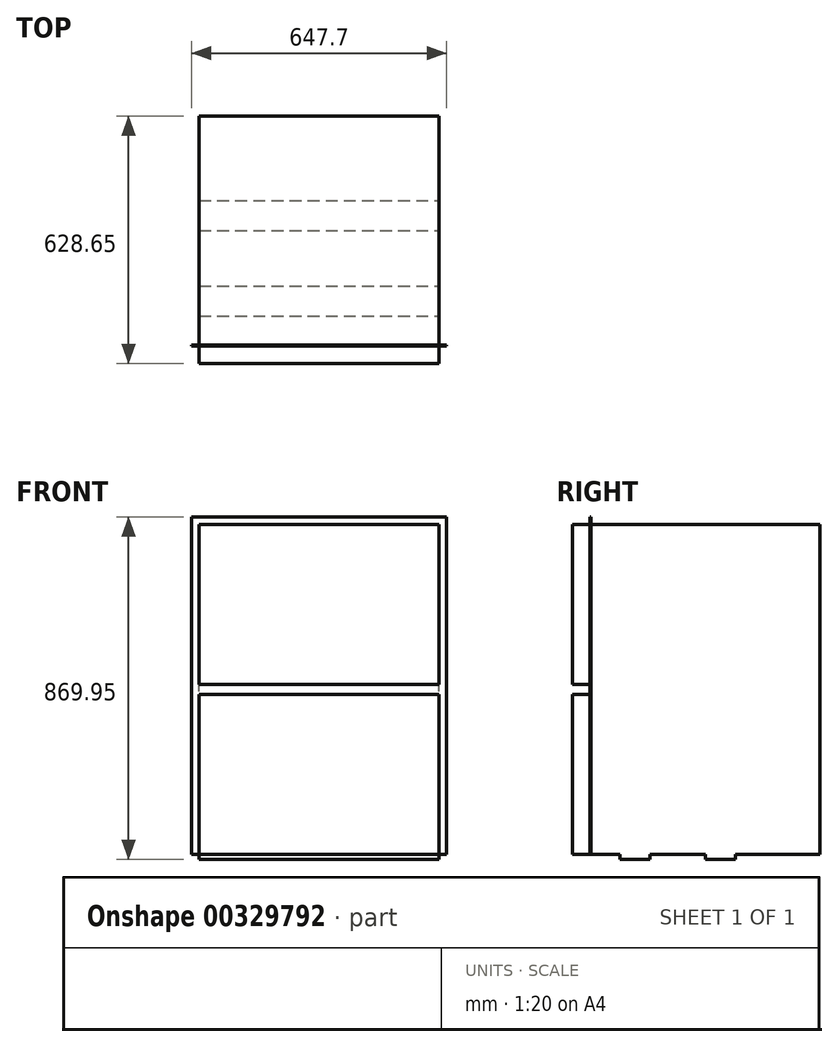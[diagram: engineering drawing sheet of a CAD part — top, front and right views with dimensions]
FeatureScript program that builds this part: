
annotation { "Feature Type Name" : "Feature", "Feature Type Description" : "" }
export const myFeature = defineFeature(function(context is Context, id is Id, definition is map)
    precondition{}
    {
        {
            var Q0;
            Q0=qCreatedBy(makeId("Front.planeOp"),FACE);
            var sketch = newSketch(context, id + "F0", { "sketchPlane" : qUnion([Q0])});
            skLineSegment(sketch, "E0.bottom", {"start": v(0, 0) * mm, "end": v(-609.6, 0) * mm});
            skLineSegment(sketch, "E0.top", {"start": v(0, 838.2) * mm, "end": v(-609.6, 838.2) * mm});
            skLineSegment(sketch, "E0.left", {"start": v(0, 0) * mm, "end": v(0, 838.2) * mm});
            skLineSegment(sketch, "E0.right", {"start": v(-609.6, 0) * mm, "end": v(-609.6, 838.2) * mm});
            skLineSegment(sketch, "E1.bottom", {"start": v(-628.65, 857.25) * mm, "end": v(19.05, 857.25) * mm});
            skLineSegment(sketch, "E1.left", {"start": v(-628.65, 857.25) * mm, "end": v(-628.65, 0) * mm});
            skLineSegment(sketch, "E1.right", {"start": v(19.05, 857.25) * mm, "end": v(19.05, 0) * mm});
            skLineSegment(sketch, "E2", {"start": v(-628.65, 0) * mm, "end": v(-609.6, 0) * mm});
            skLineSegment(sketch, "E3", {"start": v(19.05, 0) * mm, "end": v(0, 0) * mm});
            skSolve(sketch);
        }
        {
            var Q0;
            Q0=makeQuery(id+"F0.imprint","IMPRINT",FACE,{"disambiguationData":[TD([[makeQuery(id+"F0.imprint","IMPRINT",EDGE,{"derivedFrom":sQuery(id+"F0.wireOp",EDGE,"E0.bottom")}),-1.0]])]});
            extrude(context, id + "F1", {"entities" : qUnion([Q0]), "oppositeDirection" : true, "depth" : 584.2 * mm});
        }
        {
            var Q0;
            Q0=makeQuery(id+"F0.imprint","IMPRINT",FACE,{"disambiguationData":[TD([[makeQuery(id+"F0.imprint","IMPRINT",EDGE,{"derivedFrom":sQuery(id+"F0.wireOp",EDGE,"E0.top")}),-1.0]])]});
            extrude(context, id + "F2", {"entities" : qUnion([Q0]), "operationType" : NewBodyOperationType.ADD, "oppositeDirection" : true, "depth" : 2.03 * mm});
        }
        {
            var Q0;
            Q0=makeQuery(id+"F0.imprint","IMPRINT",FACE,{"disambiguationData":[TD([[makeQuery(id+"F0.imprint","IMPRINT",EDGE,{"derivedFrom":sQuery(id+"F0.wireOp",EDGE,"E0.bottom")}),-1.0]])]});
            var sketch = newSketch(context, id + "F3", { "sketchPlane" : qUnion([Q0])});
            skLineSegment(sketch, "E4.bottom", {"start": v(-609.6, 838.2) * mm, "end": v(0, 838.2) * mm});
            skLineSegment(sketch, "E4.top", {"start": v(-609.6, 431.8) * mm, "end": v(0, 431.8) * mm});
            skLineSegment(sketch, "E4.left", {"start": v(-609.6, 838.2) * mm, "end": v(-609.6, 431.8) * mm});
            skLineSegment(sketch, "E4.right", {"start": v(0, 838.2) * mm, "end": v(0, 431.8) * mm});
            skLineSegment(sketch, "E5.bottom", {"start": v(-609.6, 406.4) * mm, "end": v(0, 406.4) * mm});
            skLineSegment(sketch, "E5.top", {"start": v(-609.6, 0) * mm, "end": v(0, 0) * mm});
            skLineSegment(sketch, "E5.left", {"start": v(-609.6, 406.4) * mm, "end": v(-609.6, 0) * mm});
            skLineSegment(sketch, "E5.right", {"start": v(0, 406.4) * mm, "end": v(0, 0) * mm});
            skSolve(sketch);
        }
        {
            var Q0;
            Q0 = qSketchRegion(id + "F3", true);
            extrude(context, id + "F4", {"entities" : qUnion([Q0]), "operationType" : NewBodyOperationType.ADD, "depth" : 44.45 * mm});
        }
        {
            var Q0;
            Q0=makeQuery(id+"F4.boolean.opBoolean","MERGE",FACE,{"derivedFrom":[makeQuery(id+"F2.boolean.opBoolean","MERGE",FACE,{"derivedFrom":[makeQuery(id+"F1.opExtrude","SWEPT_FACE",FACE,{"disambiguationData":[OSD([sQuery(id+"F0.wireOp",EDGE,"E0.bottom")])]}),makeQuery(id+"F2.opExtrude","SWEPT_FACE",FACE,{"disambiguationData":[OSD([sQuery(id+"F0.wireOp",EDGE,"E2")])]}),makeQuery(id+"F2.opExtrude","SWEPT_FACE",FACE,{"disambiguationData":[OSD([sQuery(id+"F0.wireOp",EDGE,"E3")])]})]}),makeQuery(id+"F4.opExtrude","SWEPT_FACE",FACE,{"disambiguationData":[OSD([sQuery(id+"F3.wireOp",EDGE,"E5.top")])]})]});
            var sketch = newSketch(context, id + "F5", { "sketchPlane" : qUnion([Q0])});
            skLineSegment(sketch, "E6.bottom", {"start": v(-609.6, -75.96) * mm, "end": v(0, -75.96) * mm});
            skLineSegment(sketch, "E6.top", {"start": v(-609.6, -152.16) * mm, "end": v(0, -152.16) * mm});
            skLineSegment(sketch, "E6.left", {"start": v(-609.6, -75.96) * mm, "end": v(-609.6, -152.16) * mm});
            skLineSegment(sketch, "E6.right", {"start": v(0, -75.96) * mm, "end": v(0, -152.16) * mm});
            skLineSegment(sketch, "E7.bottom", {"start": v(-609.6, -293.12) * mm, "end": v(0, -293.12) * mm});
            skLineSegment(sketch, "E7.top", {"start": v(-609.6, -369.32) * mm, "end": v(0, -369.32) * mm});
            skLineSegment(sketch, "E7.left", {"start": v(-609.6, -293.12) * mm, "end": v(-609.6, -369.32) * mm});
            skLineSegment(sketch, "E7.right", {"start": v(0, -293.12) * mm, "end": v(0, -369.32) * mm});
            skSolve(sketch);
        }
        {
            var Q0;
            Q0 = qSketchRegion(id + "F5", true);
            extrude(context, id + "F6", {"entities" : qUnion([Q0]), "operationType" : NewBodyOperationType.ADD, "depth" : 12.7 * mm});
        }
    });
